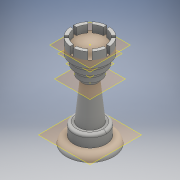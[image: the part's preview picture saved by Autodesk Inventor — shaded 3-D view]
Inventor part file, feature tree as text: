
AUTODESK INVENTOR PART (.ipt)
format: ipt  version: 2016 (Build 200138000, 138)  size: 248,832 bytes
history: native  units: mm
features: sketch x14, extrude x6, plane x6, loft x4, other x3, fillet x2
ambient origin geometry x8: Origin, YZ Plane, XZ Plane, XY Plane, X Axis, Y Axis, Z Axis, Center Point
bodies: Solid1 (feature_tree)
feature tree (35):
  extrude  "Extrusion1"  Depth=5.0mm TaperAngle=0.0deg
  plane  "Work Plane1"
  extrude  "Extrusion2"  Depth=22.0mm
  fillet  "Fillet1"  Radius=8.0mm
  sketch  "Sketch3"  dims[d7=5.0mm d8=15.0mm]
  sketch  "Sketch4"  dims[d9=25.0mm d10=10.0mm]
  sketch  "Sketch5"  dims[d11=0.0mm d12=90.0deg d13=0.0mm d14=90.0deg]
  plane  "Work Plane2"
  loft  "Loft1"
  plane  "Work Plane3"
  loft  "Loft2"
  extrude  "Extrusion3"  TaperAngle=0.0deg  [1 undecoded]
  plane  "Work Plane4"
  loft  "Loft3"
  extrude  "Extrusion4"  TaperAngle=0.0deg  [1 undecoded]
  plane  "Work Plane5"
  loft  "Loft4"
  extrude  "Extrusion7"  TaperAngle=0.0deg  [1 undecoded]
  plane  "Work Plane7"
  sketch  "Sketch17"  dims[d33=25.0mm]
  extrude  "Extrusion8"  Depth=20.0mm
  fillet  "Fillet2"  Radius=3.0mm
  sketch  "Sketch19"  dims[d36=0.0mm d37=90.0deg d38=25.0mm d45=20.5mm d59=1.0mm d60=1.0mm d71=25.0mm d72=5.0mm d73=0.0mm d74=0.0mm d80=1.0mm d81=1.0mm d82=1.0mm d83=1.0mm d84=1.0mm d85=1.0mm d86=1.0mm d87=1.0mm d93=135.0deg d94=1.0mm d95=1.0mm d97=1.0mm d98=1.0mm d99=20.5mm d100=5.0mm d101=0.0mm d102=2.0mm]
  sketch  "Sketch1"  dims[d0=32.0mm d1=5.0mm d2=0.0mm]
  sketch  "Sketch2"  dims[d3=0.0mm d4=22.0mm d5=8.0mm d6=0.0mm]
  sketch  "Sketch6"  dims[d15=3.0mm d16=15.0mm]
  sketch  "Sketch7"  dims[d17=0.0mm d18=90.0deg d19=0.0mm d20=90.0deg]
  other  "Edges1"
  sketch  "Sketch9"  dims[d21=3.0mm d22=0.0mm d23=3.0mm]
  other  "Edges2"
  sketch  "Sketch10"  dims[d24=20.0mm d25=0.0mm d26=90.0deg]
  sketch  "Sketch11"  dims[d27=0.0mm d28=90.0deg d29=20.0mm d30=3.0mm d31=0.0mm]
  other  "Edges3"
  sketch  "Sketch16"  dims[d32=3.0mm]
  sketch  "Sketch18"  dims[d34=0.0mm d35=90.0deg]
note: 3 required parameter values undecoded (feature->parameter linkage not recoverable at this tier; creation-order binding heuristic only, values carry confidence <= 0.55)
